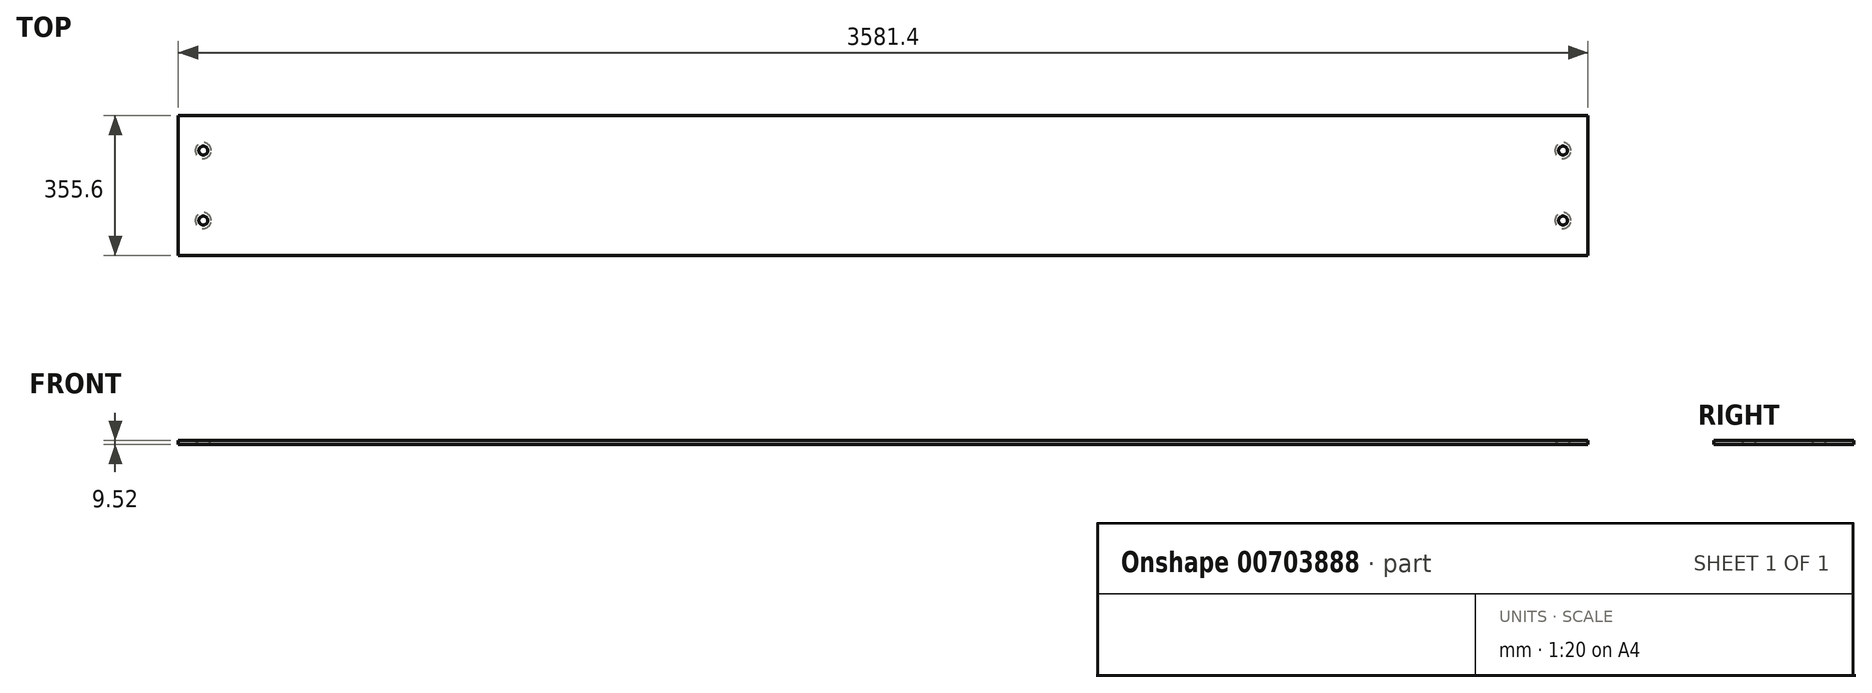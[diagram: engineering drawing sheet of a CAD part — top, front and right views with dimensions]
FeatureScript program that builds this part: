
annotation { "Feature Type Name" : "Feature", "Feature Type Description" : "" }
export const myFeature = defineFeature(function(context is Context, id is Id, definition is map)
    precondition{}
    {
        {
            var Q0;
            Q0=qCreatedBy(makeId("Right.planeOp"),FACE);
            var sketch = newSketch(context, id + "F0", { "sketchPlane" : qUnion([Q0])});
            skLineSegment(sketch, "E0.bottom", {"start": v(177.8, -4.76) * mm, "end": v(-177.8, -4.76) * mm});
            skLineSegment(sketch, "E0.top", {"start": v(177.8, 4.76) * mm, "end": v(-177.8, 4.76) * mm});
            skLineSegment(sketch, "E0.left", {"start": v(177.8, -4.76) * mm, "end": v(177.8, 4.76) * mm});
            skLineSegment(sketch, "E0.right", {"start": v(-177.8, -4.76) * mm, "end": v(-177.8, 4.76) * mm});
            skPoint(sketch, "E0.middle", {"position": v(0, 0) * mm});
            skSolve(sketch);
        }
        {
            var Q0;
            Q0=makeQuery(id+"F0.imprint","IMPRINT",FACE,{"disambiguationData":[TD([[makeQuery(id+"F0.imprint","IMPRINT",EDGE,{"derivedFrom":sQuery(id+"F0.wireOp",EDGE,"E0.bottom")}),-1.0]])]});
            extrude(context, id + "F1", {"entities" : qUnion([Q0]), "endBound" : BoundingType.SYMMETRIC, "depth" : 3352.8 * mm + 228.6 * mm, "offsetDistance" : 30.48 * mm});
        }
        {
            var Q0;
            Q0=makeQuery(id+"F1.opExtrude","SWEPT_FACE",FACE,{"disambiguationData":[OSD([sQuery(id+"F0.wireOp",EDGE,"E0.top")])]});
            var sketch = newSketch(context, id + "F2", { "sketchPlane" : qUnion([Q0])});
            skLineSegment(sketch, "E1.0.0", {"start": v(-1790.7, 177.8) * mm, "end": v(-1790.7, -177.8) * mm});
            skLineSegment(sketch, "E1.0.1", {"start": v(-1790.7, -177.8) * mm, "end": v(1790.7, -177.8) * mm});
            skLineSegment(sketch, "E1.0.2", {"start": v(1790.7, -177.8) * mm, "end": v(1790.7, 177.8) * mm});
            skLineSegment(sketch, "E1.0.3", {"start": v(1790.7, 177.8) * mm, "end": v(-1790.7, 177.8) * mm});
            skLineSegment(sketch, "E2.0", {"start": v(-1790.7, -88.9) * mm, "end": v(1790.7, -88.9) * mm});
            skLineSegment(sketch, "E3.0", {"start": v(1790.7, 88.9) * mm, "end": v(-1790.7, 88.9) * mm});
            skLineSegment(sketch, "E4.0", {"start": v(1727.2, -177.8) * mm, "end": v(1727.2, 177.8) * mm});
            skLineSegment(sketch, "E5.0", {"start": v(-1727.2, 177.8) * mm, "end": v(-1727.2, -177.8) * mm});
            skLineSegment(sketch, "E6", {"start": v(-1727.2, -88.9) * mm, "end": v(-1727.2, 88.9) * mm});
            skLineSegment(sketch, "E7", {"start": v(-1727.2, 88.9) * mm, "end": v(1727.2, 88.9) * mm});
            skLineSegment(sketch, "E8", {"start": v(1727.2, 88.9) * mm, "end": v(1727.2, -88.9) * mm});
            skCircle(sketch, "E9", {"center": v(1727.2, 88.9) * mm, "radius": 8.34 * mm});
            skCircle(sketch, "E10", {"center": v(1727.2, -88.9) * mm, "radius": 8.34 * mm});
            skCircle(sketch, "E11", {"center": v(-1727.2, 88.9) * mm, "radius": 8.34 * mm});
            skCircle(sketch, "E12", {"center": v(-1727.2, -88.9) * mm, "radius": 8.34 * mm});
            skLineSegment(sketch, "E13.0", {"start": v(-776.29, 177.8) * mm, "end": v(-776.29, -177.8) * mm});
            skLineSegment(sketch, "E14.0", {"start": v(776.29, -177.8) * mm, "end": v(776.29, 177.8) * mm});
            skLineSegment(sketch, "E15.0", {"start": v(570.65, -177.8) * mm, "end": v(570.65, 177.8) * mm});
            skLineSegment(sketch, "E16.0", {"start": v(-443.76, -177.8) * mm, "end": v(-443.76, 177.8) * mm});
            skLineSegment(sketch, "E17.0", {"start": v(-570.65, 177.8) * mm, "end": v(-570.65, -177.8) * mm});
            skSolve(sketch);
        }
        {
            var Q0;
            {var subQ1=sQuery(id+"F2.wireOp",EDGE,"E3.0");var subQ3=sQuery(id+"F2.wireOp",EDGE,"E11");var subQ4=makeQuery(id+"F2.imprint","INTERSECT",VERTEX,{"derivedFrom":[subQ1,subQ3]});Q0=makeQuery(id+"F2.imprint","IMPRINT",FACE,{"disambiguationData":[TD([[makeQuery(id+"F2.imprint","IMPRINT",EDGE,{"disambiguationData":[TD([[subQ4,-1.0]])],"derivedFrom":subQ3}),1.0]])]});}
            var Q1;
            {var subQ1=sQuery(id+"F2.wireOp",EDGE,"E6");var subQ3=sQuery(id+"F2.wireOp",EDGE,"E11");var subQ4=makeQuery(id+"F2.imprint","INTERSECT",VERTEX,{"derivedFrom":[subQ1,subQ3]});Q1=makeQuery(id+"F2.imprint","IMPRINT",FACE,{"disambiguationData":[TD([[makeQuery(id+"F2.imprint","IMPRINT",EDGE,{"disambiguationData":[TD([[subQ4,-1.0]])],"derivedFrom":subQ3}),1.0]])]});}
            var Q2;
            {var subQ1=sQuery(id+"F2.wireOp",EDGE,"E5.0");var subQ3=sQuery(id+"F2.wireOp",EDGE,"E11");var subQ4=makeQuery(id+"F2.imprint","INTERSECT",VERTEX,{"derivedFrom":[subQ1,subQ3]});Q2=makeQuery(id+"F2.imprint","IMPRINT",FACE,{"disambiguationData":[TD([[makeQuery(id+"F2.imprint","IMPRINT",EDGE,{"disambiguationData":[TD([[subQ4,1.0]])],"derivedFrom":subQ3}),1.0]])]});}
            var Q3;
            {var subQ1=sQuery(id+"F2.wireOp",EDGE,"E3.0");var subQ3=sQuery(id+"F2.wireOp",EDGE,"E11");var subQ4=makeQuery(id+"F2.imprint","INTERSECT",VERTEX,{"derivedFrom":[subQ1,subQ3]});Q3=makeQuery(id+"F2.imprint","IMPRINT",FACE,{"disambiguationData":[TD([[makeQuery(id+"F2.imprint","IMPRINT",EDGE,{"disambiguationData":[TD([[subQ4,1.0]])],"derivedFrom":subQ3}),1.0]])]});}
            var Q4;
            {var subQ1=sQuery(id+"F2.wireOp",EDGE,"E2.0");var subQ3=sQuery(id+"F2.wireOp",EDGE,"E10");var subQ4=makeQuery(id+"F2.imprint","INTERSECT",VERTEX,{"disambiguationData":[OD(1.0)],"derivedFrom":[subQ1,subQ3]});Q4=makeQuery(id+"F2.imprint","IMPRINT",FACE,{"disambiguationData":[TD([[makeQuery(id+"F2.imprint","IMPRINT",EDGE,{"disambiguationData":[TD([[subQ4,-1.0]])],"derivedFrom":subQ3}),1.0]])]});}
            var Q5;
            {var subQ1=sQuery(id+"F2.wireOp",EDGE,"E2.0");var subQ3=sQuery(id+"F2.wireOp",EDGE,"E10");var subQ4=makeQuery(id+"F2.imprint","INTERSECT",VERTEX,{"disambiguationData":[OD(0.0)],"derivedFrom":[subQ1,subQ3]});Q5=makeQuery(id+"F2.imprint","IMPRINT",FACE,{"disambiguationData":[TD([[makeQuery(id+"F2.imprint","IMPRINT",EDGE,{"disambiguationData":[TD([[subQ4,1.0]])],"derivedFrom":subQ3}),1.0]])]});}
            var Q6;
            {var subQ1=sQuery(id+"F2.wireOp",EDGE,"E2.0");var subQ3=sQuery(id+"F2.wireOp",EDGE,"E10");var subQ4=makeQuery(id+"F2.imprint","INTERSECT",VERTEX,{"disambiguationData":[OD(1.0)],"derivedFrom":[subQ1,subQ3]});Q6=makeQuery(id+"F2.imprint","IMPRINT",FACE,{"disambiguationData":[TD([[makeQuery(id+"F2.imprint","IMPRINT",EDGE,{"disambiguationData":[TD([[subQ4,1.0]])],"derivedFrom":subQ3}),1.0]])]});}
            var Q7;
            {var subQ1=sQuery(id+"F2.wireOp",EDGE,"E2.0");var subQ3=sQuery(id+"F2.wireOp",EDGE,"E10");var subQ4=makeQuery(id+"F2.imprint","INTERSECT",VERTEX,{"disambiguationData":[OD(0.0)],"derivedFrom":[subQ1,subQ3]});Q7=makeQuery(id+"F2.imprint","IMPRINT",FACE,{"disambiguationData":[TD([[makeQuery(id+"F2.imprint","IMPRINT",EDGE,{"disambiguationData":[TD([[subQ4,-1.0]])],"derivedFrom":subQ3}),1.0]])]});}
            var Q8;
            {var subQ1=sQuery(id+"F2.wireOp",EDGE,"E7");var subQ3=sQuery(id+"F2.wireOp",EDGE,"E9");var subQ4=makeQuery(id+"F2.imprint","INTERSECT",VERTEX,{"derivedFrom":[subQ1,subQ3]});Q8=makeQuery(id+"F2.imprint","IMPRINT",FACE,{"disambiguationData":[TD([[makeQuery(id+"F2.imprint","IMPRINT",EDGE,{"disambiguationData":[TD([[subQ4,-1.0]])],"derivedFrom":subQ3}),1.0]])]});}
            var Q9;
            {var subQ1=sQuery(id+"F2.wireOp",EDGE,"E4.0");var subQ3=sQuery(id+"F2.wireOp",EDGE,"E9");var subQ4=makeQuery(id+"F2.imprint","INTERSECT",VERTEX,{"derivedFrom":[subQ1,subQ3]});Q9=makeQuery(id+"F2.imprint","IMPRINT",FACE,{"disambiguationData":[TD([[makeQuery(id+"F2.imprint","IMPRINT",EDGE,{"disambiguationData":[TD([[subQ4,-1.0]])],"derivedFrom":subQ3}),1.0]])]});}
            var Q10;
            {var subQ1=sQuery(id+"F2.wireOp",EDGE,"E3.0");var subQ3=sQuery(id+"F2.wireOp",EDGE,"E9");var subQ4=makeQuery(id+"F2.imprint","INTERSECT",VERTEX,{"derivedFrom":[subQ1,subQ3]});Q10=makeQuery(id+"F2.imprint","IMPRINT",FACE,{"disambiguationData":[TD([[makeQuery(id+"F2.imprint","IMPRINT",EDGE,{"disambiguationData":[TD([[subQ4,-1.0]])],"derivedFrom":subQ3}),1.0]])]});}
            var Q11;
            {var subQ1=sQuery(id+"F2.wireOp",EDGE,"E3.0");var subQ3=sQuery(id+"F2.wireOp",EDGE,"E9");var subQ4=makeQuery(id+"F2.imprint","INTERSECT",VERTEX,{"derivedFrom":[subQ1,subQ3]});Q11=makeQuery(id+"F2.imprint","IMPRINT",FACE,{"disambiguationData":[TD([[makeQuery(id+"F2.imprint","IMPRINT",EDGE,{"disambiguationData":[TD([[subQ4,1.0]])],"derivedFrom":subQ3}),1.0]])]});}
            var Q12;
            {var subQ1=sQuery(id+"F2.wireOp",EDGE,"E2.0");var subQ3=sQuery(id+"F2.wireOp",EDGE,"E12");var subQ4=makeQuery(id+"F2.imprint","INTERSECT",VERTEX,{"disambiguationData":[OD(0.0)],"derivedFrom":[subQ1,subQ3]});Q12=makeQuery(id+"F2.imprint","IMPRINT",FACE,{"disambiguationData":[TD([[makeQuery(id+"F2.imprint","IMPRINT",EDGE,{"disambiguationData":[TD([[subQ4,1.0]])],"derivedFrom":subQ3}),1.0]])]});}
            var Q13;
            {var subQ1=sQuery(id+"F2.wireOp",EDGE,"E2.0");var subQ3=sQuery(id+"F2.wireOp",EDGE,"E12");var subQ4=makeQuery(id+"F2.imprint","INTERSECT",VERTEX,{"disambiguationData":[OD(1.0)],"derivedFrom":[subQ1,subQ3]});Q13=makeQuery(id+"F2.imprint","IMPRINT",FACE,{"disambiguationData":[TD([[makeQuery(id+"F2.imprint","IMPRINT",EDGE,{"disambiguationData":[TD([[subQ4,-1.0]])],"derivedFrom":subQ3}),1.0]])]});}
            var Q14;
            {var subQ1=sQuery(id+"F2.wireOp",EDGE,"E2.0");var subQ3=sQuery(id+"F2.wireOp",EDGE,"E12");var subQ4=makeQuery(id+"F2.imprint","INTERSECT",VERTEX,{"disambiguationData":[OD(1.0)],"derivedFrom":[subQ1,subQ3]});Q14=makeQuery(id+"F2.imprint","IMPRINT",FACE,{"disambiguationData":[TD([[makeQuery(id+"F2.imprint","IMPRINT",EDGE,{"disambiguationData":[TD([[subQ4,1.0]])],"derivedFrom":subQ3}),1.0]])]});}
            var Q15;
            {var subQ1=sQuery(id+"F2.wireOp",EDGE,"E2.0");var subQ3=sQuery(id+"F2.wireOp",EDGE,"E12");var subQ4=makeQuery(id+"F2.imprint","INTERSECT",VERTEX,{"disambiguationData":[OD(0.0)],"derivedFrom":[subQ1,subQ3]});Q15=makeQuery(id+"F2.imprint","IMPRINT",FACE,{"disambiguationData":[TD([[makeQuery(id+"F2.imprint","IMPRINT",EDGE,{"disambiguationData":[TD([[subQ4,-1.0]])],"derivedFrom":subQ3}),1.0]])]});}
            extrude(context, id + "F3", {"entities" : qUnion([Q0, Q1, Q2, Q3, Q4, Q5, Q6, Q7, Q8, Q9, Q10, Q11, Q12, Q13, Q14, Q15]), "operationType" : NewBodyOperationType.REMOVE, "oppositeDirection" : true, "depth" : 25.4 * mm, "offsetDistance" : 25.4 * mm});
        }
        {
            var Q0;
            Q0=makeQuery(id+"F3.boolean.opBoolean","INTERSECT",EDGE,{"derivedFrom":[makeQuery(id+"F1.opExtrude","SWEPT_FACE",FACE,{"disambiguationData":[OSD([sQuery(id+"F0.wireOp",EDGE,"E0.bottom")])]}),makeQuery(id+"F3.opExtrude","SWEPT_FACE",FACE,{"disambiguationData":[OSD([sQuery(id+"F2.wireOp",EDGE,"E12")])]})]});
            var Q1;
            Q1=makeQuery(id+"F3.boolean.opBoolean","INTERSECT",EDGE,{"derivedFrom":[makeQuery(id+"F1.opExtrude","SWEPT_FACE",FACE,{"disambiguationData":[OSD([sQuery(id+"F0.wireOp",EDGE,"E0.bottom")])]}),makeQuery(id+"F3.opExtrude","SWEPT_FACE",FACE,{"disambiguationData":[OSD([sQuery(id+"F2.wireOp",EDGE,"E11")])]})]});
            var Q2;
            Q2=makeQuery(id+"F3.boolean.opBoolean","INTERSECT",EDGE,{"derivedFrom":[makeQuery(id+"F1.opExtrude","SWEPT_FACE",FACE,{"disambiguationData":[OSD([sQuery(id+"F0.wireOp",EDGE,"E0.bottom")])]}),makeQuery(id+"F3.opExtrude","SWEPT_FACE",FACE,{"disambiguationData":[OSD([sQuery(id+"F2.wireOp",EDGE,"E9")])]})]});
            var Q3;
            Q3=makeQuery(id+"F3.boolean.opBoolean","INTERSECT",EDGE,{"derivedFrom":[makeQuery(id+"F1.opExtrude","SWEPT_FACE",FACE,{"disambiguationData":[OSD([sQuery(id+"F0.wireOp",EDGE,"E0.bottom")])]}),makeQuery(id+"F3.opExtrude","SWEPT_FACE",FACE,{"disambiguationData":[OSD([sQuery(id+"F2.wireOp",EDGE,"E10")])]})]});
            chamfer(context, id + "F4", {"entities" : qUnion([Q0, Q1, Q2, Q3]), "chamferType" : ChamferType.OFFSET_ANGLE, "width" : 12.7 * mm, "oppositeDirection" : false, "angle" : 43.15 * degree, "tangentPropagation" : true});
        }
    });
